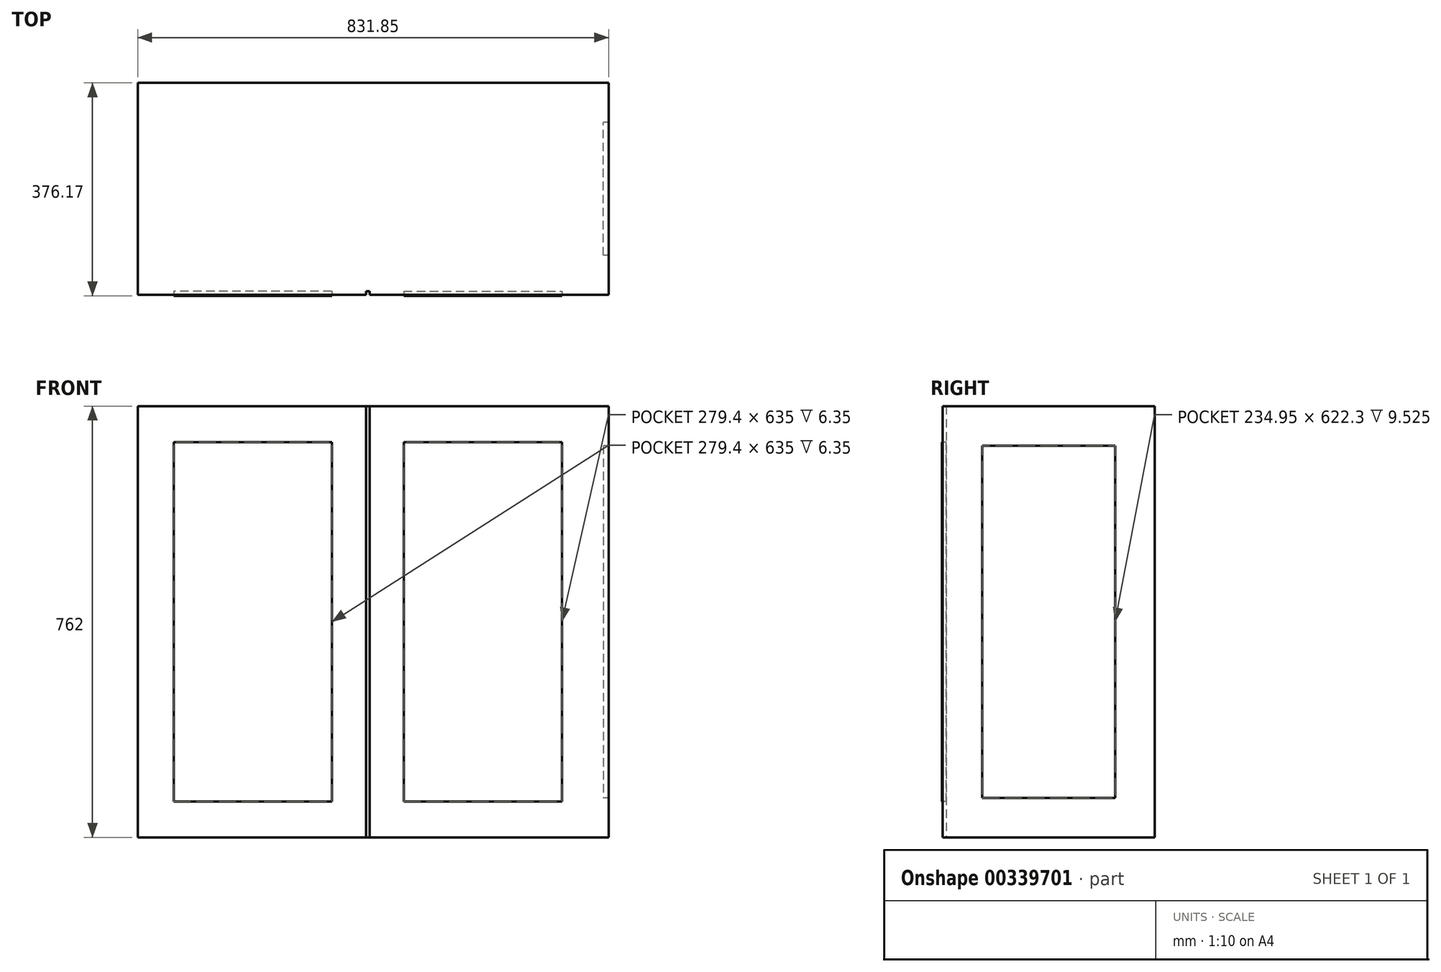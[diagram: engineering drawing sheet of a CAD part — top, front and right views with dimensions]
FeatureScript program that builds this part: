
annotation { "Feature Type Name" : "Feature", "Feature Type Description" : "" }
export const myFeature = defineFeature(function(context is Context, id is Id, definition is map)
    precondition{}
    {
        {
            var Q0;
            Q0=qCreatedBy(makeId("Front.planeOp"),FACE);
            var sketch = newSketch(context, id + "F0", { "sketchPlane" : qUnion([Q0])});
            skLineSegment(sketch, "E0.bottom", {"start": v(227.9, 0) * mm, "end": v(-178.5, 0) * mm});
            skLineSegment(sketch, "E0.top", {"start": v(227.9, 762) * mm, "end": v(-178.5, 762) * mm});
            skLineSegment(sketch, "E0.left", {"start": v(227.9, 0) * mm, "end": v(227.9, 762) * mm});
            skLineSegment(sketch, "E0.right", {"start": v(-178.5, 0) * mm, "end": v(-178.5, 762) * mm});
            skLineSegment(sketch, "E1.0", {"start": v(164.4, 698.5) * mm, "end": v(-115, 698.5) * mm});
            skLineSegment(sketch, "E1.1", {"start": v(164.4, 63.5) * mm, "end": v(164.4, 698.5) * mm});
            skLineSegment(sketch, "E1.2", {"start": v(164.4, 63.5) * mm, "end": v(-115, 63.5) * mm});
            skLineSegment(sketch, "E1.3", {"start": v(-115, 63.5) * mm, "end": v(-115, 698.5) * mm});
            skLineSegment(sketch, "E2.bottom", {"start": v(-178.5, 0) * mm, "end": v(227.9, 0) * mm});
            skLineSegment(sketch, "E3.bottom", {"start": v(-178.5, 762) * mm, "end": v(151.7, 762) * mm});
            skLineSegment(sketch, "E4.MirrorCS", {"start": v(227.9, 762) * mm, "end": v(634.3, 762) * mm});
            skLineSegment(sketch, "E5.MirrorCS", {"start": v(634.3, 762) * mm, "end": v(304.1, 762) * mm});
            skLineSegment(sketch, "E6.MirrorCS", {"start": v(227.9, 0) * mm, "end": v(634.3, 0) * mm});
            skLineSegment(sketch, "E7.MirrorCS", {"start": v(634.3, 0) * mm, "end": v(227.9, 0) * mm});
            skLineSegment(sketch, "E8.MirrorCS", {"start": v(570.8, 63.5) * mm, "end": v(570.8, 698.5) * mm});
            skLineSegment(sketch, "E9.MirrorCS", {"start": v(291.4, 63.5) * mm, "end": v(570.8, 63.5) * mm});
            skLineSegment(sketch, "E10.MirrorCS", {"start": v(291.4, 63.5) * mm, "end": v(291.4, 698.5) * mm});
            skLineSegment(sketch, "E11.MirrorCS", {"start": v(291.4, 698.5) * mm, "end": v(570.8, 698.5) * mm});
            skLineSegment(sketch, "E12.MirrorCS", {"start": v(634.3, 0) * mm, "end": v(634.3, 762) * mm});
            skLineSegment(sketch, "E13", {"start": v(224.73, 762) * mm, "end": v(224.73, 0) * mm});
            skLineSegment(sketch, "E14", {"start": v(231.08, 762) * mm, "end": v(231.08, 0) * mm});
            skSolve(sketch);
        }
        {
            var Q0;
            Q0=makeQuery(id+"F0.imprint","IMPRINT",FACE,{"disambiguationData":[TD([[makeQuery(id+"F0.imprint","IMPRINT",EDGE,{"derivedFrom":sQuery(id+"F0.wireOp",EDGE,"E1.0")}),1.0]])]});
            var Q1;
            Q1=makeQuery(id+"F0.imprint","IMPRINT",FACE,{"disambiguationData":[TD([[makeQuery(id+"F0.imprint","IMPRINT",EDGE,{"derivedFrom":sQuery(id+"F0.wireOp",EDGE,"E2.bottom")}),-1.0]])]});
            var Q2;
            Q2=makeQuery(id+"F0.imprint","IMPRINT",FACE,{"disambiguationData":[TD([[makeQuery(id+"F0.imprint","IMPRINT",EDGE,{"derivedFrom":sQuery(id+"F0.wireOp",EDGE,"E0.left")}),1.0]])]});
            var Q3;
            {var subQ0=sQuery(id+"F0.wireOp",EDGE,"E3.top");Q3=makeQuery(id+"F0.imprint","IMPRINT",FACE,{"disambiguationData":[TD([[makeQuery(id+"F0.imprint","IMPRINT",EDGE,{"derivedFrom":subQ0}),-1.0]])]});}
            var Q4;
            {var subQ0=sQuery(id+"F0.wireOp",EDGE,"E3.bottom");Q4=makeQuery(id+"F0.imprint","IMPRINT",FACE,{"disambiguationData":[TD([[makeQuery(id+"F0.imprint","IMPRINT",EDGE,{"derivedFrom":subQ0}),1.0]])]});}
            var Q5;
            Q5=makeQuery(id+"F0.imprint","IMPRINT",FACE,{"disambiguationData":[TD([[makeQuery(id+"F0.imprint","IMPRINT",EDGE,{"derivedFrom":sQuery(id+"F0.wireOp",EDGE,"E8.MirrorCS")}),1.0]])]});
            var Q6;
            {var subQ2=sQuery(id+"F0.wireOp",EDGE,"ed679ab7-f109-45c4-9ee2-0cc617b6c41517.MirrorCS");Q6=makeQuery(id+"F0.imprint","IMPRINT",FACE,{"disambiguationData":[TD([[makeQuery(id+"F0.imprint","IMPRINT",EDGE,{"derivedFrom":subQ2}),-1.0]])]});}
            var Q7;
            Q7=makeQuery(id+"F0.imprint","IMPRINT",FACE,{"disambiguationData":[TD([[makeQuery(id+"F0.imprint","IMPRINT",EDGE,{"derivedFrom":sQuery(id+"F0.wireOp",EDGE,"ed679ab7-f109-45c4-9ee2-0cc617b6c4156.MirrorCS")}),1.0]])]});
            var Q8;
            Q8=makeQuery(id+"F0.imprint","IMPRINT",FACE,{"disambiguationData":[TD([[makeQuery(id+"F0.imprint","IMPRINT",EDGE,{"derivedFrom":sQuery(id+"F0.wireOp",EDGE,"E0.left")}),-1.0]])]});
            var Q9;
            {var subQ0=sQuery(id+"F0.wireOp",EDGE,"E5.MirrorCS");Q9=makeQuery(id+"F0.imprint","IMPRINT",FACE,{"disambiguationData":[TD([[makeQuery(id+"F0.imprint","IMPRINT",EDGE,{"derivedFrom":subQ0}),-1.0]])]});}
            var Q10;
            {var subQ0=sQuery(id+"F0.wireOp",EDGE,"E0.right");Q10=makeQuery(id+"F0.imprint","IMPRINT",FACE,{"disambiguationData":[TD([[makeQuery(id+"F0.imprint","IMPRINT",EDGE,{"derivedFrom":subQ0}),-1.0]])]});}
            var Q11;
            Q11=makeQuery(id+"F0.imprint","IMPRINT",FACE,{"disambiguationData":[TD([[makeQuery(id+"F0.imprint","IMPRINT",EDGE,{"derivedFrom":sQuery(id+"F0.wireOp",EDGE,"E8.MirrorCS")}),-1.0]])]});
            extrude(context, id + "F1", {"entities" : qUnion([Q0, Q1, Q2, Q3, Q4, Q5, Q6, Q7, Q8, Q9, Q10, Q11]), "oppositeDirection" : true, "depth" : 374.65 * mm, "offsetDistance" : 25.4 * mm});
        }
        {
            var Q0;
            Q0=makeQuery(id+"F0.imprint","IMPRINT",FACE,{"disambiguationData":[TD([[makeQuery(id+"F0.imprint","IMPRINT",EDGE,{"derivedFrom":sQuery(id+"F0.wireOp",EDGE,"E1.0")}),1.0]])]});
            var Q1;
            Q1=makeQuery(id+"F0.imprint","IMPRINT",FACE,{"disambiguationData":[TD([[makeQuery(id+"F0.imprint","IMPRINT",EDGE,{"derivedFrom":sQuery(id+"F0.wireOp",EDGE,"E3.bottom")}),1.0]])]});
            var Q2;
            Q2=makeQuery(id+"F0.imprint","IMPRINT",FACE,{"disambiguationData":[TD([[makeQuery(id+"F0.imprint","IMPRINT",EDGE,{"derivedFrom":sQuery(id+"F0.wireOp",EDGE,"E8.MirrorCS")}),1.0]])]});
            var Q3;
            {var subQ0=sQuery(id+"F0.wireOp",EDGE,"E5.MirrorCS");Q3=makeQuery(id+"F0.imprint","IMPRINT",FACE,{"disambiguationData":[TD([[makeQuery(id+"F0.imprint","IMPRINT",EDGE,{"derivedFrom":subQ0}),-1.0]])]});}
            var Q4;
            {var subQ0=sQuery(id+"F0.wireOp",EDGE,"E0.left");Q4=makeQuery(id+"F0.imprint","IMPRINT",FACE,{"disambiguationData":[TD([[makeQuery(id+"F0.imprint","IMPRINT",EDGE,{"derivedFrom":subQ0}),1.0]])]});}
            var Q5;
            {var subQ0=sQuery(id+"F0.wireOp",EDGE,"E0.left");Q5=makeQuery(id+"F0.imprint","IMPRINT",FACE,{"disambiguationData":[TD([[makeQuery(id+"F0.imprint","IMPRINT",EDGE,{"derivedFrom":subQ0}),-1.0]])]});}
            extrude(context, id + "F2", {"entities" : qUnion([Q0, Q1, Q2, Q3, Q4, Q5]), "operationType" : NewBodyOperationType.REMOVE, "oppositeDirection" : true, "depth" : 6.35 * mm});
        }
        {
            var Q0;
            Q0=makeQuery(id+"F0.imprint","IMPRINT",FACE,{"disambiguationData":[TD([[makeQuery(id+"F0.imprint","IMPRINT",EDGE,{"derivedFrom":sQuery(id+"F0.wireOp",EDGE,"E1.0")}),1.0]])]});
            var Q1;
            Q1=makeQuery(id+"F0.imprint","IMPRINT",FACE,{"disambiguationData":[TD([[makeQuery(id+"F0.imprint","IMPRINT",EDGE,{"derivedFrom":sQuery(id+"F0.wireOp",EDGE,"E8.MirrorCS")}),1.0]])]});
            extrude(context, id + "F3", {"entities" : qUnion([Q0, Q1]), "depth" : 1.52 * mm, "offsetDistance" : 25.4 * mm});
        }
        {
            var Q0;
            Q0=makeQuery(id+"F1.opExtrude","SWEPT_FACE",FACE,{"disambiguationData":[OSD([sQuery(id+"F0.wireOp",EDGE,"E12.MirrorCS")])]});
            var sketch = newSketch(context, id + "F4", { "sketchPlane" : qUnion([Q0])});
            skLineSegment(sketch, "E15.bottom", {"start": v(69.85, 692.15) * mm, "end": v(304.8, 692.15) * mm});
            skLineSegment(sketch, "E15.top", {"start": v(69.85, 69.85) * mm, "end": v(304.8, 69.85) * mm});
            skLineSegment(sketch, "E15.left", {"start": v(69.85, 692.15) * mm, "end": v(69.85, 69.85) * mm});
            skLineSegment(sketch, "E15.right", {"start": v(304.8, 692.15) * mm, "end": v(304.8, 69.85) * mm});
            skSolve(sketch);
        }
        {
            var Q0;
            Q0=makeQuery(id+"F4.imprint","IMPRINT",FACE,{"disambiguationData":[TD([[makeQuery(id+"F4.imprint","IMPRINT",EDGE,{"derivedFrom":sQuery(id+"F4.wireOp",EDGE,"E15.bottom")}),1.0]])]});
            extrude(context, id + "F5", {"entities" : qUnion([Q0]), "operationType" : NewBodyOperationType.ADD, "depth" : 19.05 * mm, "offsetDistance" : 25.4 * mm});
        }
        {
            var Q0;
            Q0=makeQuery(id+"F1.opExtrude","SWEPT_FACE",FACE,{"disambiguationData":[OSD([sQuery(id+"F0.wireOp",EDGE,"E12.MirrorCS")])]});
            extrude(context, id + "F6", {"entities" : qUnion([Q0]), "operationType" : NewBodyOperationType.ADD, "depth" : 9.52 * mm, "offsetDistance" : 25.4 * mm});
        }
    });
